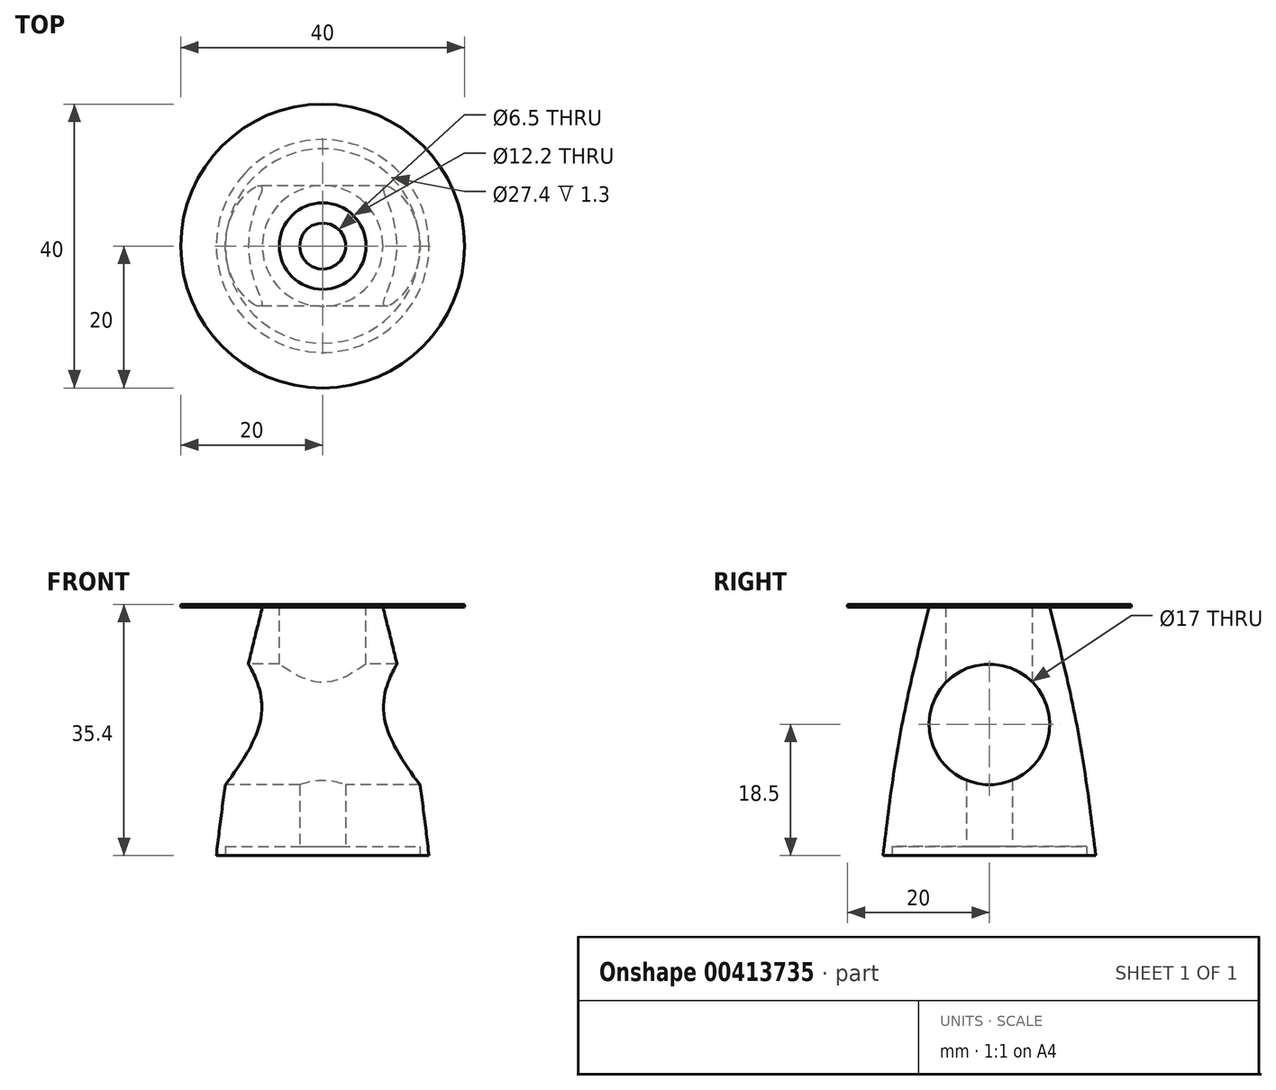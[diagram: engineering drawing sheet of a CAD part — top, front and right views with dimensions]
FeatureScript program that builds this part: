
annotation { "Feature Type Name" : "Feature", "Feature Type Description" : "" }
export const myFeature = defineFeature(function(context is Context, id is Id, definition is map)
    precondition{}
    {
        {
            var Q0;
            Q0=qCreatedBy(makeId("Right.planeOp"),FACE);
            var sketch = newSketch(context, id + "F0", { "sketchPlane" : qUnion([Q0])});
            skLineSegment(sketch, "E0", {"start": v(-15, 0) * mm, "end": v(15, 0) * mm});
            skLineSegment(sketch, "E1", {"start": v(-12.5, 17.5) * mm, "end": v(12.5, 17.5) * mm});
            skLineSegment(sketch, "E2", {"start": v(-8.5, 35) * mm, "end": v(8.5, 35) * mm});
            skFitSpline(sketch, "E3", {"points": [v(-15, 0) * mm, v(-12.5, 17.5) * mm, v(-8.5, 35) * mm], "startDerivative": vector(4.28, 35.2) * mm, "endDerivative": vector(8.7, 34.8) * mm});
            skFitSpline(sketch, "E4", {"points": [v(8.5, 35) * mm, v(12.5, 17.5) * mm, v(15, 0) * mm], "startDerivative": vector(8.7, -34.8) * mm, "endDerivative": vector(4.28, -35.2) * mm});
            skLineSegment(sketch, "E5", {"start": v(0, 35) * mm, "end": v(0, 0) * mm});
            skCircle(sketch, "E6", {"center": v(0, 18.5) * mm, "radius": 8.5 * mm});
            skSolve(sketch);
        }
        {
            var Q0;
            {var subQ0=sQuery(id+"F0.wireOp",EDGE,"E4");var subQ1=sQuery(id+"F0.wireOp",EDGE,"E0");var subQ2=makeQuery(id+"F0.imprint","INTERSECT",VERTEX,{"derivedFrom":[subQ1,subQ0]});Q0=makeQuery(id+"F0.imprint","IMPRINT",FACE,{"disambiguationData":[TD([[makeQuery(id+"F0.imprint","IMPRINT",EDGE,{"disambiguationData":[TD([[subQ2,1.0]])],"derivedFrom":subQ1}),1.0]])]});}
            var Q1;
            {var subQ0=sQuery(id+"F0.wireOp",EDGE,"E4");var subQ1=sQuery(id+"F0.wireOp",EDGE,"E1");var subQ2=makeQuery(id+"F0.imprint","INTERSECT",VERTEX,{"derivedFrom":[subQ1,subQ0]});Q1=makeQuery(id+"F0.imprint","IMPRINT",FACE,{"disambiguationData":[TD([[makeQuery(id+"F0.imprint","IMPRINT",EDGE,{"disambiguationData":[TD([[subQ2,1.0]])],"derivedFrom":subQ1}),1.0]])]});}
            var Q2;
            Q2=sQuery(id+"F0.wireOp",EDGE,"E5");
            revolve(context, id + "F1", {"entities" : qUnion([Q0, Q1]), "axis" : qUnion([Q2]), "revolveType" : RevolveType.FULL});
        }
        {
            var Q0;
            Q0=makeQuery(id+"F1.opRevolve","SWEPT_FACE",FACE,{"disambiguationData":[OSD([sQuery(id+"F0.wireOp",EDGE,"E2")])]});
            var sketch = newSketch(context, id + "F2", { "sketchPlane" : qUnion([Q0])});
            skCircle(sketch, "E7", {"center": v(0, 0) * mm, "radius": 6.1 * mm});
            skCircle(sketch, "E8", {"center": v(0, 0) * mm, "radius": 20 * mm});
            skSolve(sketch);
        }
        {
            var Q0;
            {var subQ0=sQuery(id+"F0.wireOp",EDGE,"E5");var subQ1=sQuery(id+"F0.wireOp",EDGE,"E1");var subQ2=makeQuery(id+"F0.imprint","INTERSECT",VERTEX,{"derivedFrom":[subQ1,subQ0]});Q0=makeQuery(id+"F0.imprint","IMPRINT",FACE,{"disambiguationData":[TD([[makeQuery(id+"F0.imprint","IMPRINT",EDGE,{"disambiguationData":[TD([[subQ2,-1.0]])],"derivedFrom":subQ1}),-1.0]])]});}
            var Q1;
            {var subQ0=sQuery(id+"F0.wireOp",EDGE,"E6");var subQ1=sQuery(id+"F0.wireOp",EDGE,"E1");var subQ2=makeQuery(id+"F0.imprint","INTERSECT",VERTEX,{"disambiguationData":[OD(0.0)],"derivedFrom":[subQ1,subQ0]});Q1=makeQuery(id+"F0.imprint","IMPRINT",FACE,{"disambiguationData":[TD([[makeQuery(id+"F0.imprint","IMPRINT",EDGE,{"disambiguationData":[TD([[subQ2,-1.0]])],"derivedFrom":subQ1}),-1.0]])]});}
            var Q2;
            {var subQ0=sQuery(id+"F0.wireOp",EDGE,"E6");var subQ1=sQuery(id+"F0.wireOp",EDGE,"E1");var subQ2=makeQuery(id+"F0.imprint","INTERSECT",VERTEX,{"disambiguationData":[OD(0.0)],"derivedFrom":[subQ1,subQ0]});Q2=makeQuery(id+"F0.imprint","IMPRINT",FACE,{"disambiguationData":[TD([[makeQuery(id+"F0.imprint","IMPRINT",EDGE,{"disambiguationData":[TD([[subQ2,-1.0]])],"derivedFrom":subQ1}),1.0]])]});}
            var Q3;
            {var subQ0=sQuery(id+"F0.wireOp",EDGE,"E5");var subQ1=sQuery(id+"F0.wireOp",EDGE,"E1");var subQ2=makeQuery(id+"F0.imprint","INTERSECT",VERTEX,{"derivedFrom":[subQ1,subQ0]});Q3=makeQuery(id+"F0.imprint","IMPRINT",FACE,{"disambiguationData":[TD([[makeQuery(id+"F0.imprint","IMPRINT",EDGE,{"disambiguationData":[TD([[subQ2,-1.0]])],"derivedFrom":subQ1}),1.0]])]});}
            extrude(context, id + "F3", {"entities" : qUnion([Q0, Q1, Q2, Q3]), "operationType" : NewBodyOperationType.REMOVE, "endBound" : BoundingType.SYMMETRIC, "depth" : 30 * mm});
        }
        {
            var Q0;
            Q0=makeQuery(id+"F2.imprint","IMPRINT",FACE,{"disambiguationData":[TD([[makeQuery(id+"F2.imprint","IMPRINT",EDGE,{"derivedFrom":sQuery(id+"F2.wireOp",EDGE,"E7")}),1.0]])]});
            extrude(context, id + "F4", {"entities" : qUnion([Q0]), "operationType" : NewBodyOperationType.REMOVE, "oppositeDirection" : true, "depth" : 20 * mm});
        }
        {
            var Q0;
            Q0=makeQuery(id+"F1.opRevolve","SWEPT_FACE",FACE,{"disambiguationData":[OSD([sQuery(id+"F0.wireOp",EDGE,"E0")])]});
            var sketch = newSketch(context, id + "F5", { "sketchPlane" : qUnion([Q0])});
            skCircle(sketch, "E9", {"center": v(0, 0) * mm, "radius": 3.25 * mm});
            skCircle(sketch, "E10", {"center": v(0, 0) * mm, "radius": 13.7 * mm});
            skSolve(sketch);
        }
        {
            var Q0;
            Q0=makeQuery(id+"F5.imprint","IMPRINT",FACE,{"disambiguationData":[TD([[makeQuery(id+"F5.imprint","IMPRINT",EDGE,{"derivedFrom":sQuery(id+"F5.wireOp",EDGE,"E9")}),1.0]])]});
            extrude(context, id + "F6", {"entities" : qUnion([Q0]), "operationType" : NewBodyOperationType.REMOVE, "oppositeDirection" : true, "depth" : 20 * mm});
        }
        {
            var Q0;
            Q0=makeQuery(id+"F5.imprint","IMPRINT",FACE,{"disambiguationData":[TD([[makeQuery(id+"F5.imprint","IMPRINT",EDGE,{"derivedFrom":sQuery(id+"F5.wireOp",EDGE,"E9")}),-1.0]])]});
            extrude(context, id + "F7", {"entities" : qUnion([Q0]), "operationType" : NewBodyOperationType.REMOVE, "oppositeDirection" : true, "depth" : 1.3 * mm});
        }
        {
            var Q0;
            Q0=makeQuery(id+"F2.imprint","IMPRINT",FACE,{"disambiguationData":[TD([[makeQuery(id+"F2.imprint","IMPRINT",EDGE,{"derivedFrom":sQuery(id+"F2.wireOp",EDGE,"E8")}),1.0]])]});
            var Q1;
            Q1=makeQuery(id+"F2.imprint","IMPRINT",FACE,{"disambiguationData":[TD([[makeQuery(id+"F2.imprint","IMPRINT",EDGE,{"derivedFrom":sQuery(id+"F2.wireOp",EDGE,"E7")}),-1.0]])]});
            extrude(context, id + "F8", {"entities" : qUnion([Q0, Q1]), "operationType" : NewBodyOperationType.ADD, "depth" : 0.4 * mm});
        }
    });
